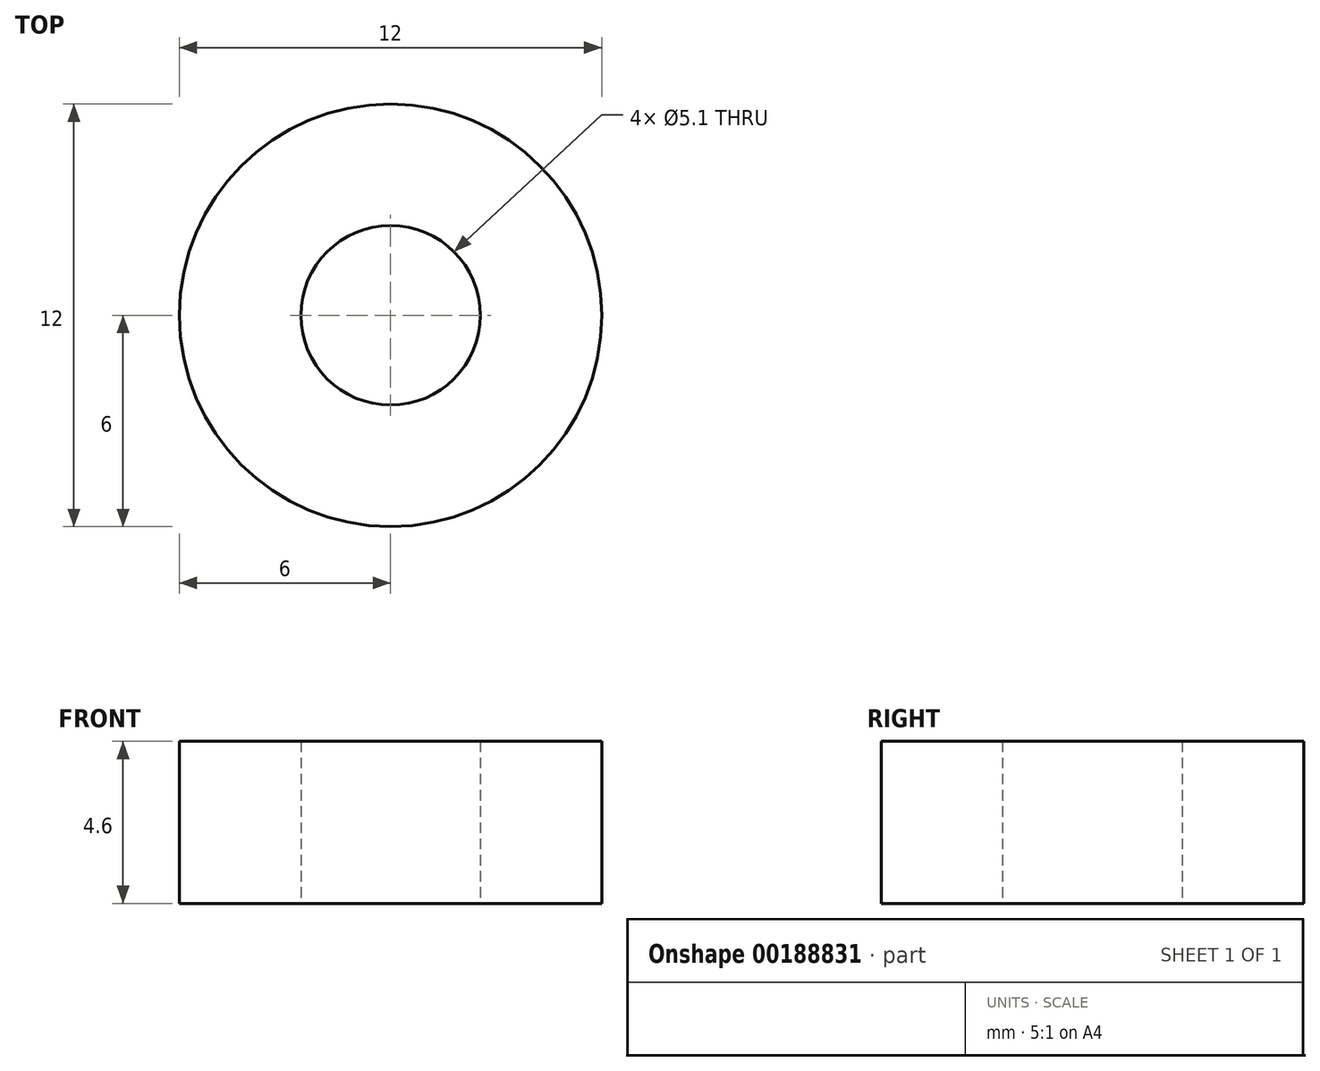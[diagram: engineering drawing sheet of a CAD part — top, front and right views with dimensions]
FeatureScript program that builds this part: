
annotation { "Feature Type Name" : "Feature", "Feature Type Description" : "" }
export const myFeature = defineFeature(function(context is Context, id is Id, definition is map)
    precondition{}
    {
        {
            var Q0;
            Q0=qCreatedBy(makeId("Top.planeOp"),FACE);
            var sketch = newSketch(context, id + "F0", { "sketchPlane" : qUnion([Q0])});
            skCircle(sketch, "E0", {"center": v(0, 0) * mm, "radius": 6 * mm});
            skCircle(sketch, "E1", {"center": v(0, 0) * mm, "radius": 2.55 * mm});
            skSolve(sketch);
        }
        {
            var Q0;
            Q0=makeQuery(id+"F0.imprint","IMPRINT",FACE,{"disambiguationData":[TD([[makeQuery(id+"F0.imprint","IMPRINT",EDGE,{"derivedFrom":sQuery(id+"F0.wireOp",EDGE,"E0")}),1.0]])]});
            extrude(context, id + "F1", {"entities" : qUnion([Q0]), "depth" : 4.6 * mm, "offsetDistance" : 25 * mm});
        }
    });
